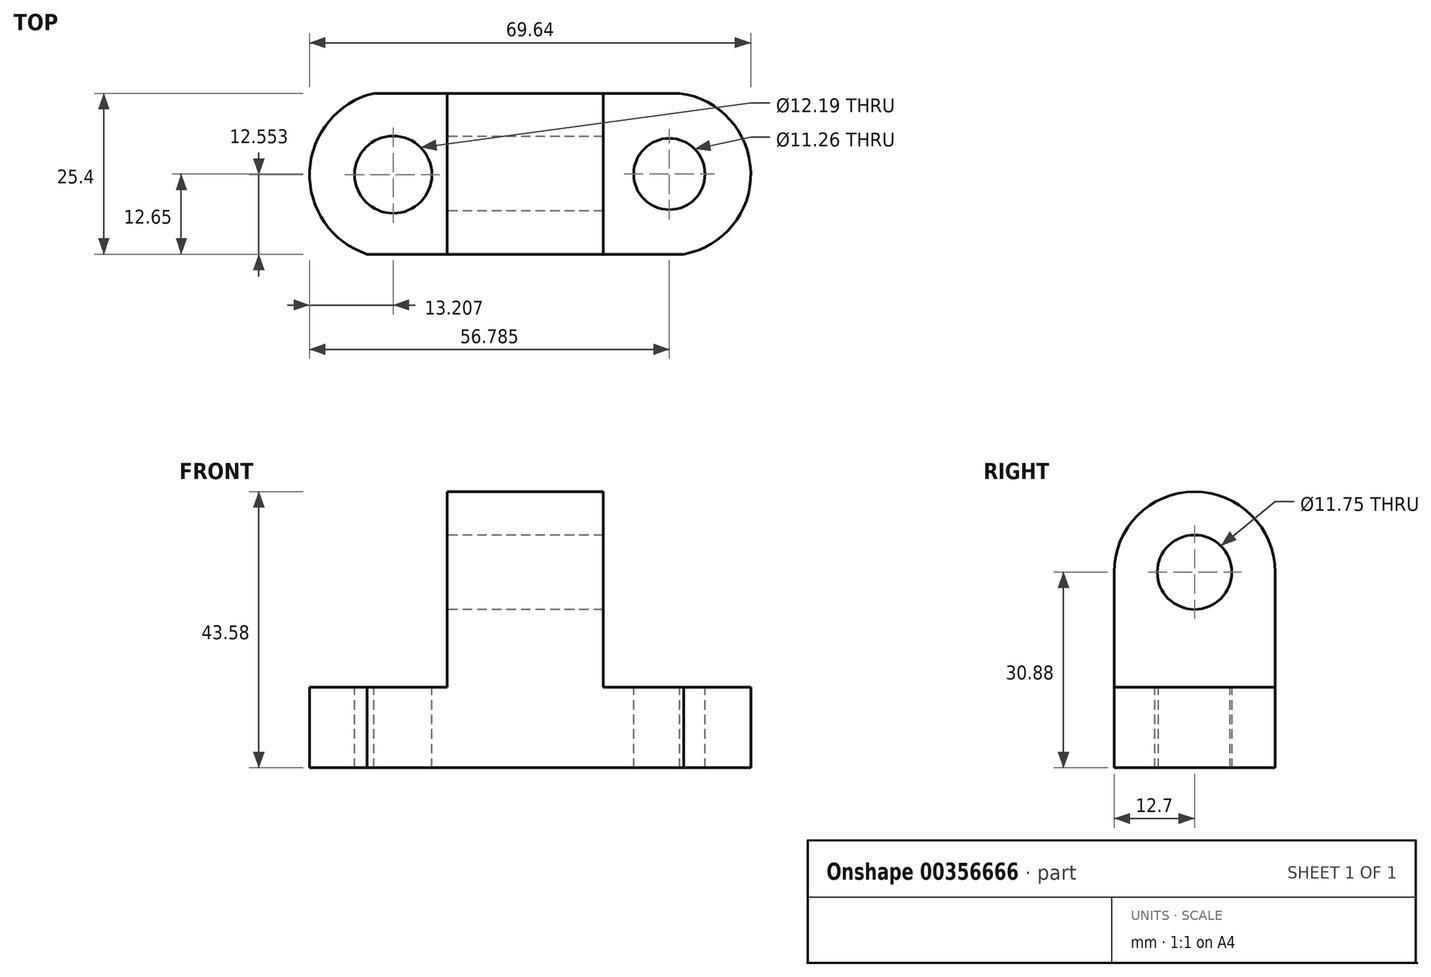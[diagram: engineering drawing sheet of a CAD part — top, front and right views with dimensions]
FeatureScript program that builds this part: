
annotation { "Feature Type Name" : "Feature", "Feature Type Description" : "" }
export const myFeature = defineFeature(function(context is Context, id is Id, definition is map)
    precondition{}
    {
        {
            var Q0;
            Q0=qCreatedBy(makeId("Front.planeOp"),FACE);
            var sketch = newSketch(context, id + "F0", { "sketchPlane" : qUnion([Q0])});
            skLineSegment(sketch, "E0.bottom", {"start": v(-21.87, -30.88) * mm, "end": v(47.98, -30.88) * mm});
            skLineSegment(sketch, "E0.top", {"start": v(-21.87, 13.57) * mm, "end": v(47.98, 13.57) * mm});
            skLineSegment(sketch, "E0.left", {"start": v(-21.87, -30.88) * mm, "end": v(-21.87, 13.57) * mm});
            skLineSegment(sketch, "E0.right", {"start": v(47.98, -30.88) * mm, "end": v(47.98, 13.57) * mm});
            skSolve(sketch);
        }
        {
            var Q0;
            Q0=makeQuery(id+"F0.imprint","IMPRINT",FACE,{"disambiguationData":[TD([[makeQuery(id+"F0.imprint","IMPRINT",EDGE,{"derivedFrom":sQuery(id+"F0.wireOp",EDGE,"E0.bottom")}),1.0]])]});
            extrude(context, id + "F1", {"entities" : qUnion([Q0]), "depth" : 25.4 * mm});
        }
        {
            var Q0;
            Q0=makeQuery(id+"F1.opExtrude","SWEPT_FACE",FACE,{"disambiguationData":[OSD([sQuery(id+"F0.wireOp",EDGE,"E0.top")])]});
            var sketch = newSketch(context, id + "F2", { "sketchPlane" : qUnion([Q0])});
            skArc(sketch, "E1", {"start": v(37.33, -25.4) * mm, "mid": v(47.75, -10.8) * mm, "end": v(33.41, 0) * mm});
            skArc(sketch, "E2", {"start": v(-5.48, 0) * mm, "mid": v(-21.73, -13.39) * mm, "end": v(-4.44, -25.4) * mm});
            skSolve(sketch);
        }
        {
            var Q0;
            {var subQ1=sQuery(id+"F0.wireOp",EDGE,"E0.top");var subQ6=makeQuery(id+"F1.opExtrude","SWEPT_EDGE",EDGE,{"disambiguationData":[OSD([subQ1,sQuery(id+"F0.wireOp",EDGE,"E0.left")])]});Q0=makeQuery(id+"F2.imprint","IMPRINT",FACE,{"disambiguationData":[TD([[makeQuery(id+"F2.imprint","IMPRINT",EDGE,{"derivedFrom":subQ6}),-1.0]])]});}
            var Q1;
            {var subQ1=sQuery(id+"F0.wireOp",EDGE,"E0.top");var subQ6=makeQuery(id+"F1.opExtrude","SWEPT_EDGE",EDGE,{"disambiguationData":[OSD([subQ1,sQuery(id+"F0.wireOp",EDGE,"E0.right")])]});Q1=makeQuery(id+"F2.imprint","IMPRINT",FACE,{"disambiguationData":[TD([[makeQuery(id+"F2.imprint","IMPRINT",EDGE,{"derivedFrom":subQ6}),1.0]])]});}
            extrude(context, id + "F3", {"entities" : qUnion([Q0, Q1]), "operationType" : NewBodyOperationType.REMOVE, "oppositeDirection" : true, "depth" : 25.4 * mm});
        }
        {
            var Q0;
            Q0=makeQuery(id+"F3.boolean.opBoolean","COPY",FACE,{"derivedFrom":makeQuery(id+"F3.opExtrude","CAP_FACE",FACE,{"disambiguationData":[OSD([sQuery(id+"F0.wireOp",EDGE,"E0.top"),sQuery(id+"F0.wireOp",EDGE,"E0.left"),sQuery(id+"F2.wireOp",EDGE,"E2")])],"isStart":false})});
            var Q1;
            Q1=makeQuery(id+"F3.boolean.opBoolean","COPY",FACE,{"derivedFrom":makeQuery(id+"F3.opExtrude","CAP_FACE",FACE,{"disambiguationData":[OSD([sQuery(id+"F0.wireOp",EDGE,"E0.top"),sQuery(id+"F0.wireOp",EDGE,"E0.right"),sQuery(id+"F2.wireOp",EDGE,"E1")])],"isStart":false})});
            extrude(context, id + "F4", {"entities" : qUnion([Q0, Q1]), "operationType" : NewBodyOperationType.REMOVE, "oppositeDirection" : true, "depth" : 25.4 * mm});
        }
        {
            var Q0;
            Q0=makeQuery(id+"F1.opExtrude","SWEPT_FACE",FACE,{"disambiguationData":[OSD([sQuery(id+"F0.wireOp",EDGE,"E0.top")])]});
            var sketch = newSketch(context, id + "F5", { "sketchPlane" : qUnion([Q0])});
            skLineSegment(sketch, "E3.bottom", {"start": v(-12.63, -25.4) * mm, "end": v(0, -25.4) * mm});
            skLineSegment(sketch, "E3.top", {"start": v(-12.63, 0) * mm, "end": v(0, 0) * mm});
            skLineSegment(sketch, "E3.left", {"start": v(-12.63, -25.4) * mm, "end": v(-12.63, 0) * mm});
            skLineSegment(sketch, "E3.right", {"start": v(0, -25.4) * mm, "end": v(0, 0) * mm});
            skLineSegment(sketch, "E4.bottom", {"start": v(37.33, -25.4) * mm, "end": v(24.63, -25.4) * mm});
            skLineSegment(sketch, "E4.top", {"start": v(37.33, 0) * mm, "end": v(24.63, 0) * mm});
            skLineSegment(sketch, "E4.left", {"start": v(37.33, -25.4) * mm, "end": v(37.33, 0) * mm});
            skLineSegment(sketch, "E4.right", {"start": v(24.63, -25.4) * mm, "end": v(24.63, 0) * mm});
            skSolve(sketch);
        }
        {
            var Q0;
            {var subQ0=sQuery(id+"F5.wireOp",EDGE,"E3.left");var subQ1=makeQuery(id+"F3.boolean.opBoolean","COPY",EDGE,{"derivedFrom":makeQuery(id+"F3.opExtrude","CAP_EDGE",EDGE,{"disambiguationData":[OSD([sQuery(id+"F2.wireOp",EDGE,"E2")])],"isStart":true})});var subQ3=makeQuery(id+"F5.imprint","INTERSECT",VERTEX,{"derivedFrom":[subQ1,subQ0]});Q0=makeQuery(id+"F5.imprint","IMPRINT",FACE,{"disambiguationData":[TD([[makeQuery(id+"F5.imprint","IMPRINT",EDGE,{"disambiguationData":[TD([[subQ3,1.0]])],"derivedFrom":subQ0}),1.0]])]});}
            var Q1;
            {var subQ1=sQuery(id+"F5.wireOp",EDGE,"E3.bottom");Q1=makeQuery(id+"F5.imprint","IMPRINT",FACE,{"disambiguationData":[TD([[makeQuery(id+"F5.imprint","IMPRINT",EDGE,{"derivedFrom":subQ1}),1.0]])]});}
            var Q2;
            {var subQ1=sQuery(id+"F5.wireOp",EDGE,"E4.bottom");Q2=makeQuery(id+"F5.imprint","IMPRINT",FACE,{"disambiguationData":[TD([[makeQuery(id+"F5.imprint","IMPRINT",EDGE,{"derivedFrom":subQ1}),1.0]])]});}
            var Q3;
            {var subQ0=sQuery(id+"F5.wireOp",EDGE,"E4.left");var subQ1=makeQuery(id+"F3.boolean.opBoolean","COPY",EDGE,{"derivedFrom":makeQuery(id+"F3.opExtrude","CAP_EDGE",EDGE,{"disambiguationData":[OSD([sQuery(id+"F2.wireOp",EDGE,"E1")])],"isStart":true})});var subQ3=makeQuery(id+"F5.imprint","INTERSECT",VERTEX,{"derivedFrom":[subQ1,subQ0]});Q3=makeQuery(id+"F5.imprint","IMPRINT",FACE,{"disambiguationData":[TD([[makeQuery(id+"F5.imprint","IMPRINT",EDGE,{"disambiguationData":[TD([[subQ3,1.0]])],"derivedFrom":subQ0}),-1.0]])]});}
            extrude(context, id + "F6", {"entities" : qUnion([Q0, Q1, Q2, Q3]), "operationType" : NewBodyOperationType.REMOVE, "oppositeDirection" : true, "depth" : 31.75 * mm});
        }
        {
            var Q0;
            Q0=makeQuery(id+"F6.boolean.opBoolean","COPY",FACE,{"derivedFrom":makeQuery(id+"F6.opExtrude","CAP_FACE",FACE,{"disambiguationData":[OSD([sQuery(id+"F2.wireOp",EDGE,"E2"),sQuery(id+"F5.wireOp",EDGE,"E3.bottom"),sQuery(id+"F5.wireOp",EDGE,"E3.top"),sQuery(id+"F5.wireOp",EDGE,"E3.right")])],"isStart":false})});
            var sketch = newSketch(context, id + "F7", { "sketchPlane" : qUnion([Q0])});
            skCircle(sketch, "E5", {"center": v(-8.53, -12.85) * mm, "radius": 6.1 * mm});
            skSolve(sketch);
        }
        {
            var Q0;
            Q0=makeQuery(id+"F7.imprint","IMPRINT",FACE,{"disambiguationData":[TD([[makeQuery(id+"F7.imprint","IMPRINT",EDGE,{"derivedFrom":sQuery(id+"F7.wireOp",EDGE,"E5")}),1.0]])]});
            extrude(context, id + "F8", {"entities" : qUnion([Q0]), "operationType" : NewBodyOperationType.REMOVE, "oppositeDirection" : true, "depth" : 25.4 * mm});
        }
        {
            var Q0;
            Q0=makeQuery(id+"F6.boolean.opBoolean","COPY",FACE,{"derivedFrom":makeQuery(id+"F6.opExtrude","CAP_FACE",FACE,{"disambiguationData":[OSD([sQuery(id+"F2.wireOp",EDGE,"E1"),sQuery(id+"F5.wireOp",EDGE,"E4.bottom"),sQuery(id+"F5.wireOp",EDGE,"E4.top"),sQuery(id+"F5.wireOp",EDGE,"E4.right")])],"isStart":false})});
            var sketch = newSketch(context, id + "F9", { "sketchPlane" : qUnion([Q0])});
            skCircle(sketch, "E6", {"center": v(35.05, -12.75) * mm, "radius": 5.63 * mm});
            skSolve(sketch);
        }
        {
            var Q0;
            Q0=makeQuery(id+"F9.imprint","IMPRINT",FACE,{"disambiguationData":[TD([[makeQuery(id+"F9.imprint","IMPRINT",EDGE,{"derivedFrom":sQuery(id+"F9.wireOp",EDGE,"E6")}),1.0]])]});
            extrude(context, id + "F10", {"entities" : qUnion([Q0]), "operationType" : NewBodyOperationType.REMOVE, "oppositeDirection" : true, "depth" : 25.4 * mm});
        }
        {
            var Q0;
            Q0=makeQuery(id+"F6.boolean.opBoolean","COPY",FACE,{"derivedFrom":makeQuery(id+"F6.opExtrude","SWEPT_FACE",FACE,{"disambiguationData":[OSD([sQuery(id+"F5.wireOp",EDGE,"E3.right")])]})});
            var sketch = newSketch(context, id + "F11", { "sketchPlane" : qUnion([Q0])});
            skLineSegment(sketch, "E7", {"start": v(0, -18.18) * mm, "end": v(25.4, -18.18) * mm});
            skLineSegment(sketch, "E8", {"start": v(25.4, -18.18) * mm, "end": v(25.4, 0) * mm});
            skArc(sketch, "E9", {"start": v(25.4, 0) * mm, "mid": v(12.7, 12.7) * mm, "end": v(0, 0) * mm});
            skSolve(sketch);
        }
        {
            var Q0;
            {var subQ0=sQuery(id+"F11.wireOp",EDGE,"E9");Q0=makeQuery(id+"F11.imprint","IMPRINT",FACE,{"disambiguationData":[TD([[makeQuery(id+"F11.imprint","IMPRINT",EDGE,{"derivedFrom":subQ0}),-1.0]])]});}
            extrude(context, id + "F12", {"entities" : qUnion([Q0]), "operationType" : NewBodyOperationType.REMOVE, "oppositeDirection" : true, "depth" : 25.4 * mm});
        }
        {
            var Q0;
            Q0=makeQuery(id+"F6.boolean.opBoolean","COPY",FACE,{"derivedFrom":makeQuery(id+"F6.opExtrude","SWEPT_FACE",FACE,{"disambiguationData":[OSD([sQuery(id+"F5.wireOp",EDGE,"E3.right")])]})});
            var sketch = newSketch(context, id + "F13", { "sketchPlane" : qUnion([Q0])});
            skCircle(sketch, "E10", {"center": v(12.7, 0) * mm, "radius": 5.88 * mm});
            skSolve(sketch);
        }
        {
            var Q0;
            Q0=makeQuery(id+"F13.imprint","IMPRINT",FACE,{"disambiguationData":[TD([[makeQuery(id+"F13.imprint","IMPRINT",EDGE,{"derivedFrom":sQuery(id+"F13.wireOp",EDGE,"E10")}),1.0]])]});
            extrude(context, id + "F14", {"entities" : qUnion([Q0]), "operationType" : NewBodyOperationType.REMOVE, "oppositeDirection" : true, "depth" : 25.4 * mm});
        }
    });
